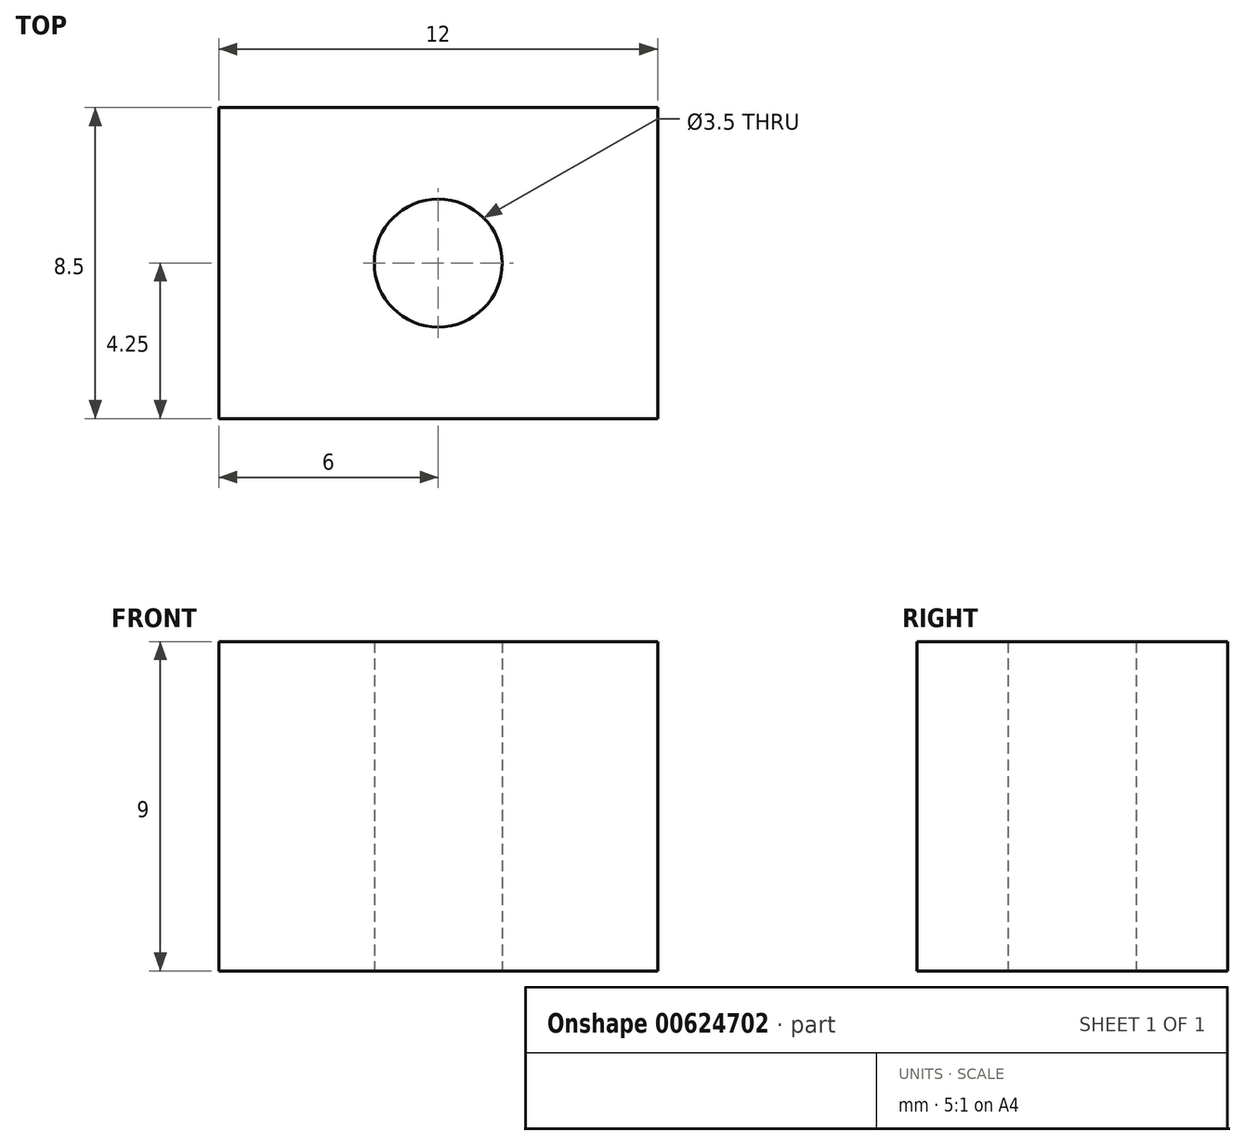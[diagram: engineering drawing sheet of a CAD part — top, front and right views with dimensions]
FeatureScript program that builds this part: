
annotation { "Feature Type Name" : "Feature", "Feature Type Description" : "" }
export const myFeature = defineFeature(function(context is Context, id is Id, definition is map)
    precondition{}
    {
        {
            var Q0;
            Q0=qCreatedBy(makeId("Top.planeOp"),FACE);
            var sketch = newSketch(context, id + "F0", { "sketchPlane" : qUnion([Q0])});
            skLineSegment(sketch, "E0.bottom", {"start": v(-6, 4.25) * mm, "end": v(6, 4.25) * mm});
            skLineSegment(sketch, "E0.top", {"start": v(-6, -4.25) * mm, "end": v(6, -4.25) * mm});
            skLineSegment(sketch, "E0.left", {"start": v(-6, 4.25) * mm, "end": v(-6, -4.25) * mm});
            skLineSegment(sketch, "E0.right", {"start": v(6, 4.25) * mm, "end": v(6, -4.25) * mm});
            skCircle(sketch, "E1", {"center": v(0, 0) * mm, "radius": 1.75 * mm});
            skSolve(sketch);
        }
        {
            var Q0;
            Q0 = qSketchRegion(id + "F0", true);
            extrude(context, id + "F1", {"entities" : qUnion([Q0]), "depth" : 9 * mm, "offsetDistance" : 25 * mm});
        }
    });
